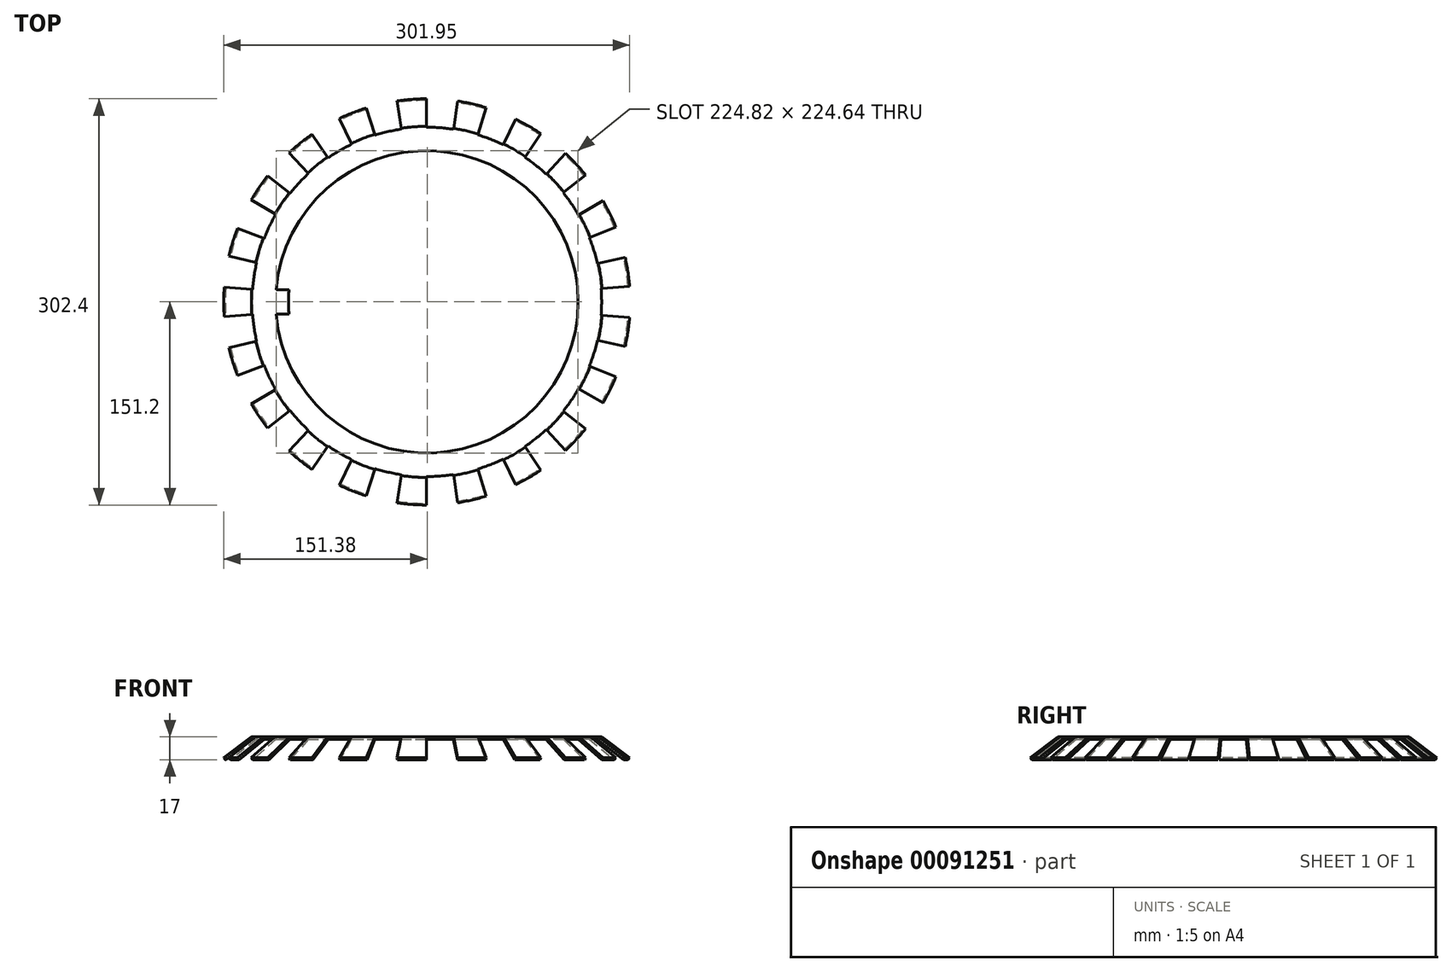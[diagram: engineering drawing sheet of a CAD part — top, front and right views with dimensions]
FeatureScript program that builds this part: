
annotation { "Feature Type Name" : "Feature", "Feature Type Description" : "" }
export const myFeature = defineFeature(function(context is Context, id is Id, definition is map)
    precondition{}
    {
        {
            var Q0;
            Q0=qCreatedBy(makeId("Front.planeOp"),FACE);
            var sketch = newSketch(context, id + "F0", { "sketchPlane" : qUnion([Q0])});
            skLineSegment(sketch, "E0", {"start": v(-103, 17) * mm, "end": v(-130.67, 17) * mm});
            skLineSegment(sketch, "E1", {"start": v(-130.67, 17) * mm, "end": v(-151.2, 1.6) * mm});
            skLineSegment(sketch, "E2", {"start": v(-151.2, 1.6) * mm, "end": v(-150, 0) * mm});
            skLineSegment(sketch, "E3", {"start": v(-150, 0) * mm, "end": v(-130, 15) * mm});
            skLineSegment(sketch, "E4", {"start": v(-130, 15) * mm, "end": v(-103, 15) * mm});
            skLineSegment(sketch, "E5", {"start": v(-103, 15) * mm, "end": v(-103, 17) * mm});
            skLineSegment(sketch, "E6", {"start": v(0, 53.8) * mm, "end": v(0, -50.35) * mm, "construction": true});
            skSolve(sketch);
        }
        {
            var Q0;
            Q0=makeQuery(id+"F0.imprint","IMPRINT",FACE,{"disambiguationData":[TD([[makeQuery(id+"F0.imprint","IMPRINT",EDGE,{"derivedFrom":sQuery(id+"F0.wireOp",EDGE,"E0")}),1.0]])]});
            var Q1;
            Q1=sQuery(id+"F0.wireOp",EDGE,"E6");
            revolve(context, id + "F1", {"entities" : qUnion([Q0]), "axis" : qUnion([Q1]), "revolveType" : RevolveType.FULL});
        }
        {
            var Q0;
            Q0=qCreatedBy(makeId("Top.planeOp"),FACE);
            var sketch = newSketch(context, id + "F2", { "sketchPlane" : qUnion([Q0])});
            skArc(sketch, "E7", {"start": v(-112.14, -9) * mm, "mid": v(112.5, 0) * mm, "end": v(-112.14, 9) * mm});
            skLineSegment(sketch, "E8.bottom", {"start": v(-94.22, 9) * mm, "end": v(-112.14, 9) * mm});
            skLineSegment(sketch, "E8.top", {"start": v(-94.22, -9) * mm, "end": v(-112.14, -9) * mm});
            skLineSegment(sketch, "E8.left", {"start": v(-94.22, 9) * mm, "end": v(-94.22, -9) * mm});
            skPoint(sketch, "E8.middle", {"position": v(-112.5, 0) * mm});
            skPoint(sketch, "E8.right.start.orphan", {"position": v(-130.78, 9) * mm});
            skPoint(sketch, "E9.orphan", {"position": v(-130.78, -9) * mm});
            skSolve(sketch);
        }
        {
            var Q0;
            Q0=makeQuery(id+"F2.imprint","IMPRINT",FACE,{"disambiguationData":[TD([[makeQuery(id+"F2.imprint","IMPRINT",EDGE,{"derivedFrom":sQuery(id+"F2.wireOp",EDGE,"E7")}),1.0]])]});
            extrude(context, id + "F3", {"entities" : qUnion([Q0]), "operationType" : NewBodyOperationType.REMOVE, "depth" : 25 * mm});
        }
        {
            var Q0;
            Q0=qCreatedBy(makeId("Top.planeOp"),FACE);
            var sketch = newSketch(context, id + "F4", { "sketchPlane" : qUnion([Q0])});
            skLineSegment(sketch, "E10", {"start": v(129.6, 10.06) * mm, "end": v(154.53, 12) * mm});
            skLineSegment(sketch, "E11", {"start": v(154.53, 12) * mm, "end": v(154.53, -12) * mm});
            skLineSegment(sketch, "E12", {"start": v(154.53, -12) * mm, "end": v(129.6, -10.06) * mm});
            skLineSegment(sketch, "E13.1.0", {"start": v(120.89, 47.82) * mm, "end": v(144.13, 57.02) * mm});
            skLineSegment(sketch, "E13.1.1", {"start": v(144.13, 57.02) * mm, "end": v(151.2, 34.08) * mm});
            skLineSegment(sketch, "E13.1.2", {"start": v(151.2, 34.08) * mm, "end": v(126.82, 28.59) * mm});
            skLineSegment(sketch, "E13.2.0", {"start": v(101.42, 81.33) * mm, "end": v(120.92, 96.97) * mm});
            skLineSegment(sketch, "E13.2.1", {"start": v(120.92, 96.97) * mm, "end": v(134.44, 77.14) * mm});
            skLineSegment(sketch, "E13.2.2", {"start": v(134.44, 77.14) * mm, "end": v(112.76, 64.7) * mm});
            skPoint(sketch, "E13.center", {"position": v(0, 0) * mm});
            skLineSegment(sketch, "E14.1.3.0", {"start": v(72.94, 107.6) * mm, "end": v(86.97, 128.3) * mm});
            skLineSegment(sketch, "E14.3.3.0", {"start": v(86.97, 128.3) * mm, "end": v(105.73, 113.34) * mm});
            skLineSegment(sketch, "E14.6.3.0", {"start": v(105.73, 113.34) * mm, "end": v(88.68, 95.06) * mm});
            skLineSegment(sketch, "E14.1.4.0", {"start": v(37.98, 124.33) * mm, "end": v(45.29, 148.24) * mm});
            skLineSegment(sketch, "E14.3.4.0", {"start": v(45.29, 148.24) * mm, "end": v(67.63, 139.47) * mm});
            skLineSegment(sketch, "E14.6.4.0", {"start": v(67.63, 139.47) * mm, "end": v(56.72, 116.97) * mm});
            skLineSegment(sketch, "E14.1.5.0", {"start": v(-0.35, 130) * mm, "end": v(-0.42, 155) * mm});
            skLineSegment(sketch, "E14.3.5.0", {"start": v(-0.42, 155) * mm, "end": v(23.51, 153.2) * mm});
            skLineSegment(sketch, "E14.6.5.0", {"start": v(23.51, 153.2) * mm, "end": v(19.72, 128.5) * mm});
            skLineSegment(sketch, "E14.1.6.0", {"start": v(-38.65, 124.12) * mm, "end": v(-46.09, 148) * mm});
            skLineSegment(sketch, "E14.3.6.0", {"start": v(-46.09, 148) * mm, "end": v(-22.69, 153.33) * mm});
            skLineSegment(sketch, "E14.6.6.0", {"start": v(-22.69, 153.33) * mm, "end": v(-19.03, 128.6) * mm});
            skLineSegment(sketch, "E14.1.7.0", {"start": v(-73.52, 107.21) * mm, "end": v(-87.66, 127.83) * mm});
            skLineSegment(sketch, "E14.3.7.0", {"start": v(-87.66, 127.83) * mm, "end": v(-66.88, 139.83) * mm});
            skLineSegment(sketch, "E14.6.7.0", {"start": v(-66.88, 139.83) * mm, "end": v(-56.09, 117.28) * mm});
            skLineSegment(sketch, "E14.1.8.0", {"start": v(-101.86, 80.78) * mm, "end": v(-121.44, 96.31) * mm});
            skLineSegment(sketch, "E14.3.8.0", {"start": v(-121.44, 96.31) * mm, "end": v(-105.12, 113.9) * mm});
            skLineSegment(sketch, "E14.6.8.0", {"start": v(-105.12, 113.9) * mm, "end": v(-88.17, 95.53) * mm});
            skLineSegment(sketch, "E14.1.9.0", {"start": v(-121.14, 47.17) * mm, "end": v(-144.44, 56.24) * mm});
            skLineSegment(sketch, "E14.3.9.0", {"start": v(-144.44, 56.24) * mm, "end": v(-134.02, 77.86) * mm});
            skLineSegment(sketch, "E14.6.9.0", {"start": v(-134.02, 77.86) * mm, "end": v(-112.4, 65.3) * mm});
            skLineSegment(sketch, "E15.1.10.0", {"start": v(-129.66, 9.37) * mm, "end": v(-154.6, 11.17) * mm});
            skLineSegment(sketch, "E15.3.10.0", {"start": v(-154.6, 11.17) * mm, "end": v(-151.02, 34.9) * mm});
            skLineSegment(sketch, "E15.6.10.0", {"start": v(-151.02, 34.9) * mm, "end": v(-126.66, 29.27) * mm});
            skLineSegment(sketch, "E15.1.11.0", {"start": v(-126.66, -29.27) * mm, "end": v(-151.02, -34.9) * mm});
            skLineSegment(sketch, "E15.3.11.0", {"start": v(-151.02, -34.9) * mm, "end": v(-154.6, -11.17) * mm});
            skLineSegment(sketch, "E15.6.11.0", {"start": v(-154.6, -11.17) * mm, "end": v(-129.66, -9.37) * mm});
            skLineSegment(sketch, "E15.1.12.0", {"start": v(-112.4, -65.3) * mm, "end": v(-134.02, -77.86) * mm});
            skLineSegment(sketch, "E15.3.12.0", {"start": v(-134.02, -77.86) * mm, "end": v(-144.44, -56.24) * mm});
            skLineSegment(sketch, "E15.6.12.0", {"start": v(-144.44, -56.24) * mm, "end": v(-121.14, -47.17) * mm});
            skLineSegment(sketch, "E15.1.13.0", {"start": v(-88.17, -95.53) * mm, "end": v(-105.12, -113.9) * mm});
            skLineSegment(sketch, "E15.3.13.0", {"start": v(-105.12, -113.9) * mm, "end": v(-121.44, -96.31) * mm});
            skLineSegment(sketch, "E15.6.13.0", {"start": v(-121.44, -96.31) * mm, "end": v(-101.86, -80.78) * mm});
            skLineSegment(sketch, "E15.1.14.0", {"start": v(-56.09, -117.28) * mm, "end": v(-66.88, -139.83) * mm});
            skLineSegment(sketch, "E15.3.14.0", {"start": v(-66.88, -139.83) * mm, "end": v(-87.66, -127.83) * mm});
            skLineSegment(sketch, "E15.6.14.0", {"start": v(-87.66, -127.83) * mm, "end": v(-73.52, -107.21) * mm});
            skLineSegment(sketch, "E15.1.15.0", {"start": v(-19.03, -128.6) * mm, "end": v(-22.69, -153.33) * mm});
            skLineSegment(sketch, "E15.3.15.0", {"start": v(-22.69, -153.33) * mm, "end": v(-46.09, -148) * mm});
            skLineSegment(sketch, "E15.6.15.0", {"start": v(-46.09, -148) * mm, "end": v(-38.65, -124.12) * mm});
            skLineSegment(sketch, "E15.1.16.0", {"start": v(19.72, -128.5) * mm, "end": v(23.51, -153.2) * mm});
            skLineSegment(sketch, "E15.3.16.0", {"start": v(23.51, -153.2) * mm, "end": v(-0.42, -155) * mm});
            skLineSegment(sketch, "E15.6.16.0", {"start": v(-0.42, -155) * mm, "end": v(-0.35, -130) * mm});
            skLineSegment(sketch, "E15.1.17.0", {"start": v(56.72, -116.97) * mm, "end": v(67.63, -139.47) * mm});
            skLineSegment(sketch, "E15.3.17.0", {"start": v(67.63, -139.47) * mm, "end": v(45.29, -148.24) * mm});
            skLineSegment(sketch, "E15.6.17.0", {"start": v(45.29, -148.24) * mm, "end": v(37.98, -124.33) * mm});
            skLineSegment(sketch, "E15.1.18.0", {"start": v(88.68, -95.06) * mm, "end": v(105.73, -113.34) * mm});
            skLineSegment(sketch, "E15.3.18.0", {"start": v(105.73, -113.34) * mm, "end": v(86.97, -128.3) * mm});
            skLineSegment(sketch, "E15.6.18.0", {"start": v(86.97, -128.3) * mm, "end": v(72.94, -107.6) * mm});
            skLineSegment(sketch, "E15.1.19.0", {"start": v(112.76, -64.7) * mm, "end": v(134.44, -77.14) * mm});
            skLineSegment(sketch, "E15.3.19.0", {"start": v(134.44, -77.14) * mm, "end": v(120.92, -96.97) * mm});
            skLineSegment(sketch, "E15.6.19.0", {"start": v(120.92, -96.97) * mm, "end": v(101.42, -81.33) * mm});
            skLineSegment(sketch, "E16.1.20.0", {"start": v(126.82, -28.59) * mm, "end": v(151.2, -34.08) * mm});
            skLineSegment(sketch, "E16.3.20.0", {"start": v(151.2, -34.08) * mm, "end": v(144.13, -57.02) * mm});
            skLineSegment(sketch, "E16.6.20.0", {"start": v(144.13, -57.02) * mm, "end": v(120.89, -47.82) * mm});
            skArc(sketch, "E17", {"start": v(88.68, 95.06) * mm, "mid": v(81.05, 101.64) * mm, "end": v(72.94, 107.6) * mm});
            skArc(sketch, "E18.trimOffspring", {"start": v(112.76, 64.7) * mm, "mid": v(107.41, 73.23) * mm, "end": v(101.42, 81.33) * mm});
            skArc(sketch, "E19.trimOffspring", {"start": v(126.82, 28.59) * mm, "mid": v(124.22, 38.32) * mm, "end": v(120.89, 47.82) * mm});
            skArc(sketch, "E20.trimOffspring", {"start": v(129.6, -10.06) * mm, "mid": v(130, 0) * mm, "end": v(129.6, 10.06) * mm});
            skArc(sketch, "E21.trimOffspring", {"start": v(122.11, -44.6) * mm, "mid": v(124.73, -36.63) * mm, "end": v(126.84, -28.5) * mm});
            skArc(sketch, "E22.trimOffspring", {"start": v(120.89, -47.82) * mm, "mid": v(124.22, -38.32) * mm, "end": v(126.82, -28.59) * mm});
            skArc(sketch, "E23.trimOffspring", {"start": v(101.42, -81.33) * mm, "mid": v(107.41, -73.23) * mm, "end": v(112.76, -64.7) * mm});
            skArc(sketch, "E24.trimOffspring", {"start": v(72.94, -107.6) * mm, "mid": v(81.05, -101.64) * mm, "end": v(88.68, -95.06) * mm});
            skArc(sketch, "E25.trimOffspring", {"start": v(37.98, -124.33) * mm, "mid": v(47.5, -121.01) * mm, "end": v(56.72, -116.97) * mm});
            skArc(sketch, "E26.trimOffspring", {"start": v(-0.35, -130) * mm, "mid": v(9.71, -129.64) * mm, "end": v(19.72, -128.5) * mm});
            skArc(sketch, "E27.trimOffspring", {"start": v(-38.65, -124.12) * mm, "mid": v(-28.93, -126.74) * mm, "end": v(-19.03, -128.6) * mm});
            skArc(sketch, "E28.trimOffspring", {"start": v(-73.52, -107.21) * mm, "mid": v(-65, -112.58) * mm, "end": v(-56.09, -117.28) * mm});
            skArc(sketch, "E29.trimOffspring", {"start": v(-101.86, -80.78) * mm, "mid": v(-95.3, -88.42) * mm, "end": v(-88.17, -95.53) * mm});
            skArc(sketch, "E30.trimOffspring", {"start": v(-121.14, -47.17) * mm, "mid": v(-117.13, -56.4) * mm, "end": v(-112.4, -65.3) * mm});
            skArc(sketch, "E31.trimOffspring", {"start": v(-129.66, -9.37) * mm, "mid": v(-128.55, -19.38) * mm, "end": v(-126.66, -29.27) * mm});
            skArc(sketch, "E32.trimOffspring", {"start": v(-126.66, 29.27) * mm, "mid": v(-128.55, 19.38) * mm, "end": v(-129.66, 9.37) * mm});
            skArc(sketch, "E33.trimOffspring", {"start": v(-112.4, 65.3) * mm, "mid": v(-117.13, 56.4) * mm, "end": v(-121.14, 47.17) * mm});
            skArc(sketch, "E34.trimOffspring", {"start": v(-88.17, 95.53) * mm, "mid": v(-95.3, 88.42) * mm, "end": v(-101.86, 80.78) * mm});
            skArc(sketch, "E35.trimOffspring", {"start": v(-56.09, 117.28) * mm, "mid": v(-65, 112.58) * mm, "end": v(-73.52, 107.21) * mm});
            skArc(sketch, "E36.trimOffspring", {"start": v(-19.03, 128.6) * mm, "mid": v(-28.93, 126.74) * mm, "end": v(-38.65, 124.12) * mm});
            skArc(sketch, "E37.trimOffspring", {"start": v(19.72, 128.5) * mm, "mid": v(9.71, 129.64) * mm, "end": v(-0.35, 130) * mm});
            skArc(sketch, "E38.trimOffspring", {"start": v(56.72, 116.97) * mm, "mid": v(47.5, 121.01) * mm, "end": v(37.98, 124.33) * mm});
            skSolve(sketch);
        }
        {
            var Q0;
            Q0 = qSketchRegion(id + "F4", true);
            extrude(context, id + "F5", {"entities" : qUnion([Q0]), "operationType" : NewBodyOperationType.REMOVE, "depth" : 25 * mm});
        }
    });
